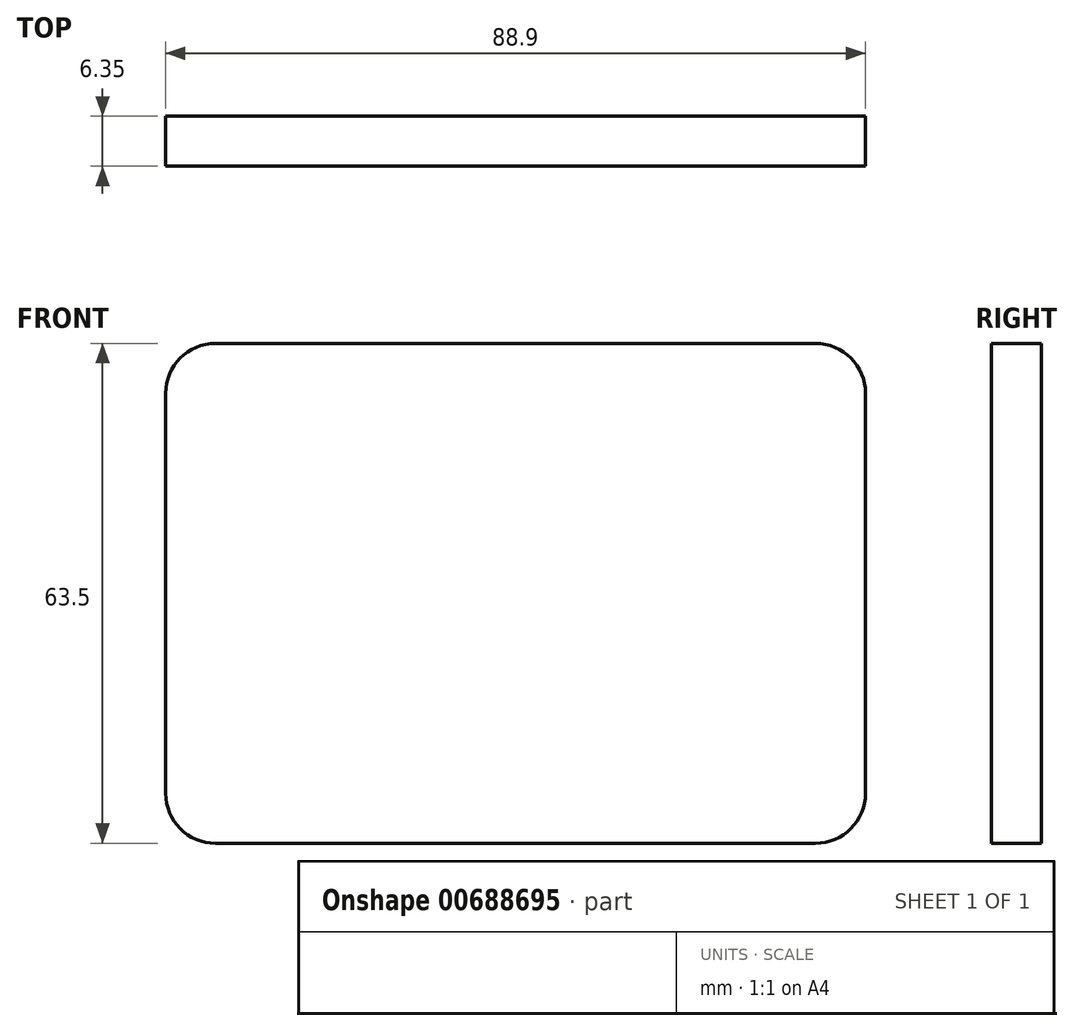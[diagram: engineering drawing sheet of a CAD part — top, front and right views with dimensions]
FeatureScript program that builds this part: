
annotation { "Feature Type Name" : "Feature", "Feature Type Description" : "" }
export const myFeature = defineFeature(function(context is Context, id is Id, definition is map)
    precondition{}
    {
        {
            var Q0;
            Q0=qCreatedBy(makeId("Front.planeOp"),FACE);
            var sketch = newSketch(context, id + "F0", { "sketchPlane" : qUnion([Q0])});
            skLineSegment(sketch, "E0.bottom", {"start": v(-38.7, 29.08) * mm, "end": v(37.5, 29.08) * mm});
            skLineSegment(sketch, "E0.top", {"start": v(-38.7, -34.42) * mm, "end": v(37.5, -34.42) * mm});
            skLineSegment(sketch, "E0.left", {"start": v(-45.06, 22.73) * mm, "end": v(-45.06, -28.07) * mm});
            skLineSegment(sketch, "E0.right", {"start": v(43.84, 22.73) * mm, "end": v(43.84, -28.07) * mm});
            skPoint(sketch, "E1.visualSharp", {"position": v(-45.06, 29.08) * mm});
            skArc(sketch, "E1.filletArc", {"start": v(-38.7, 29.08) * mm, "mid": v(-43.2, 27.22) * mm, "end": v(-45.06, 22.73) * mm});
            skPoint(sketch, "E2.visualSharp", {"position": v(43.84, 29.08) * mm});
            skArc(sketch, "E2.filletArc", {"start": v(43.84, 22.73) * mm, "mid": v(41.98, 27.22) * mm, "end": v(37.5, 29.08) * mm});
            skPoint(sketch, "E3.visualSharp", {"position": v(43.84, -34.42) * mm});
            skArc(sketch, "E3.filletArc", {"start": v(37.5, -34.42) * mm, "mid": v(41.98, -32.56) * mm, "end": v(43.84, -28.07) * mm});
            skPoint(sketch, "E4.visualSharp", {"position": v(-45.06, -34.42) * mm});
            skArc(sketch, "E4.filletArc", {"start": v(-45.06, -28.07) * mm, "mid": v(-43.2, -32.56) * mm, "end": v(-38.7, -34.42) * mm});
            skSolve(sketch);
        }
        {
            var Q0;
            Q0 = qSketchRegion(id + "F0", true);
            extrude(context, id + "F1", {"entities" : qUnion([Q0]), "depth" : 6.35 * mm, "offsetDistance" : 25.4 * mm});
        }
    });
